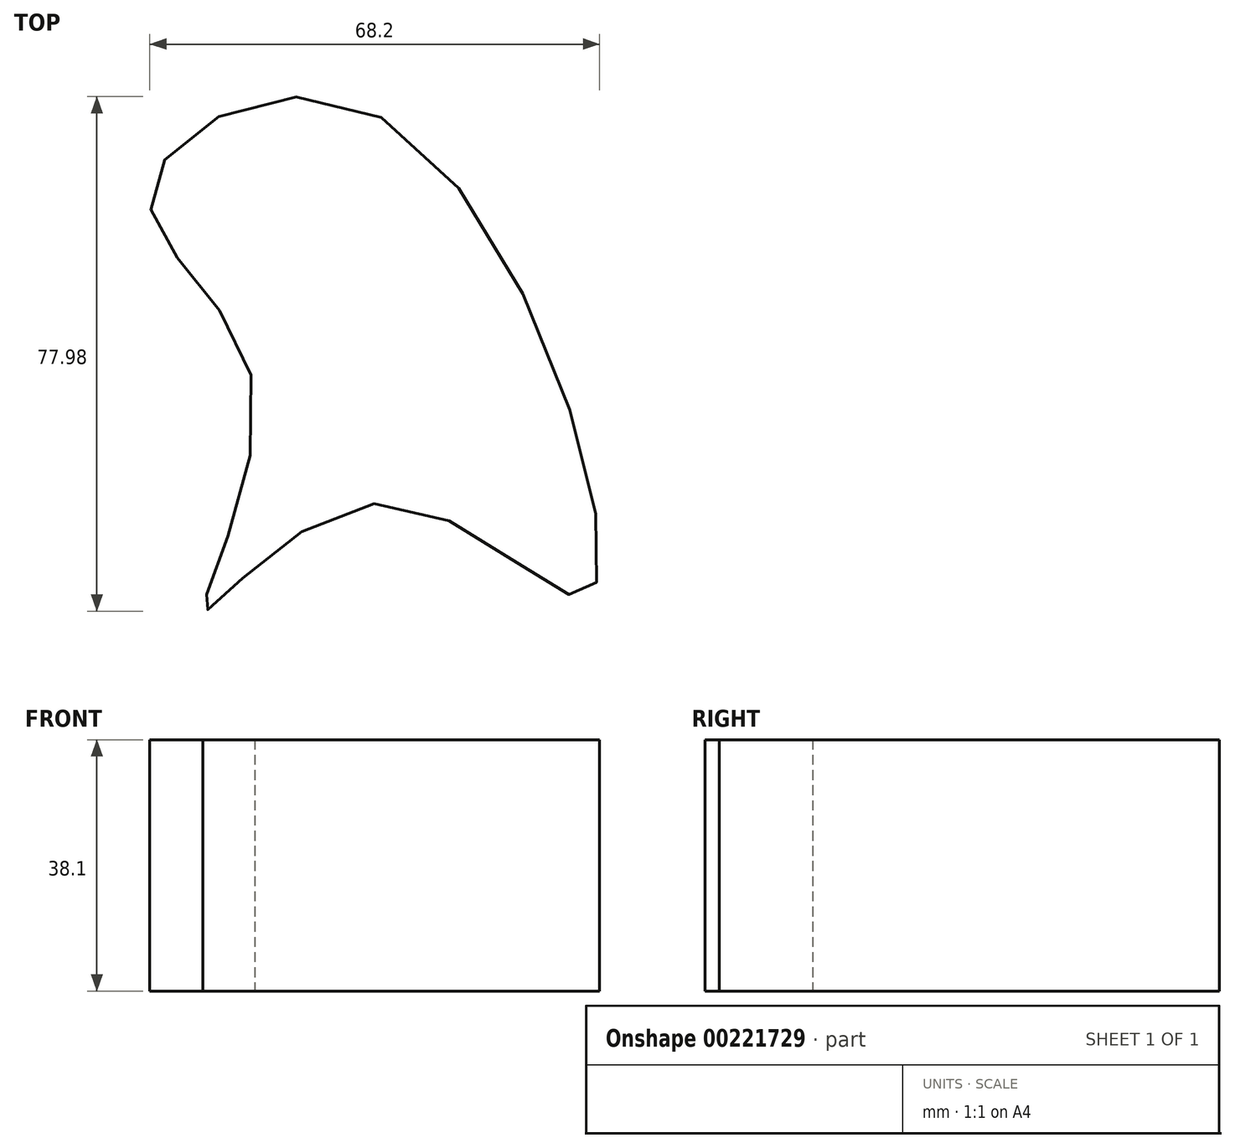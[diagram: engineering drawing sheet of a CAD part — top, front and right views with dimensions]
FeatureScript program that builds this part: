
annotation { "Feature Type Name" : "Feature", "Feature Type Description" : "" }
export const myFeature = defineFeature(function(context is Context, id is Id, definition is map)
    precondition{}
    {
        {
            var Q0;
            Q0=qCreatedBy(makeId("Top.planeOp"),FACE);
            var sketch = newSketch(context, id + "F0", { "sketchPlane" : qUnion([Q0])});
            skFitSpline(sketch, "E0", {"points": [v(0, 40.57) * mm, v(-35.01, 29.09) * mm, v(-19.45, 0) * mm, v(-26.86, -34.27) * mm, v(0, -17.97) * mm, v(31.68, -31.68) * mm, v(0, 40.57) * mm]});
            skSolve(sketch);
        }
        {
            var Q0;
            Q0=makeQuery(id+"F0.imprint","IMPRINT",FACE,{"disambiguationData":[TD([[makeQuery(id+"F0.imprint","IMPRINT",EDGE,{"derivedFrom":sQuery(id+"F0.wireOp",EDGE,"E0")}),1.0]])]});
            extrude(context, id + "F1", {"entities" : qUnion([Q0]), "depth" : 38.1 * mm});
        }
    });
